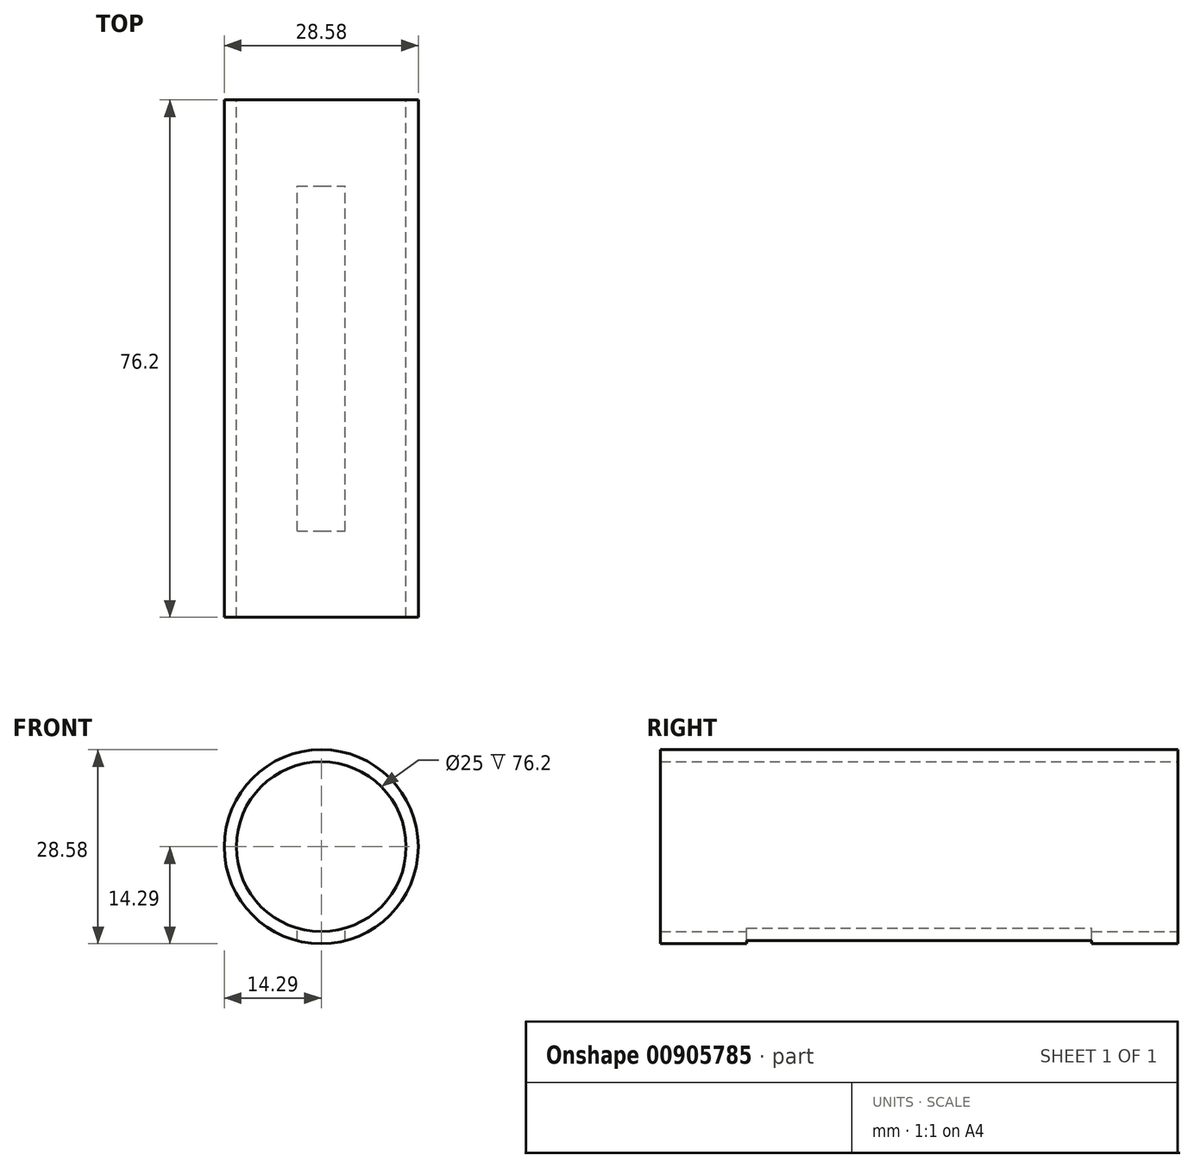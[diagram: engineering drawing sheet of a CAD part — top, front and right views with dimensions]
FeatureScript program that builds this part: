
annotation { "Feature Type Name" : "Feature", "Feature Type Description" : "" }
export const myFeature = defineFeature(function(context is Context, id is Id, definition is map)
    precondition{}
    {
        {
            var Q0;
            Q0=qCreatedBy(makeId("Front.planeOp"),FACE);
            var sketch = newSketch(context, id + "F0", { "sketchPlane" : qUnion([Q0])});
            skCircle(sketch, "E0", {"center": v(0, 0) * mm, "radius": 14.29 * mm});
            skCircle(sketch, "E1", {"center": v(0, 0) * mm, "radius": 12.5 * mm});
            skSolve(sketch);
        }
        {
            var Q0;
            Q0 = qSketchRegion(id + "F0", true);
            extrude(context, id + "F1", {"entities" : qUnion([Q0]), "depth" : 76.2 * mm, "offsetDistance" : 25.4 * mm});
        }
        {
            var Q0;
            Q0=qCreatedBy(makeId("Top.planeOp"),FACE);
            var sketch = newSketch(context, id + "F2", { "sketchPlane" : qUnion([Q0])});
            skLineSegment(sketch, "E2.bottom", {"start": v(-3.5, -12.7) * mm, "end": v(3.5, -12.7) * mm});
            skLineSegment(sketch, "E2.top", {"start": v(-3.5, -63.5) * mm, "end": v(3.5, -63.5) * mm});
            skLineSegment(sketch, "E2.left", {"start": v(-3.5, -12.7) * mm, "end": v(-3.5, -63.5) * mm});
            skLineSegment(sketch, "E2.right", {"start": v(3.5, -12.7) * mm, "end": v(3.5, -63.5) * mm});
            skSolve(sketch);
        }
        {
            var Q0;
            Q0 = qSketchRegion(id + "F2", true);
            extrude(context, id + "F3", {"entities" : qUnion([Q0]), "operationType" : NewBodyOperationType.REMOVE, "endBound" : BoundingType.THROUGH_ALL, "oppositeDirection" : true, "depth" : 25.4 * mm, "offsetDistance" : 25.4 * mm});
        }
    });
